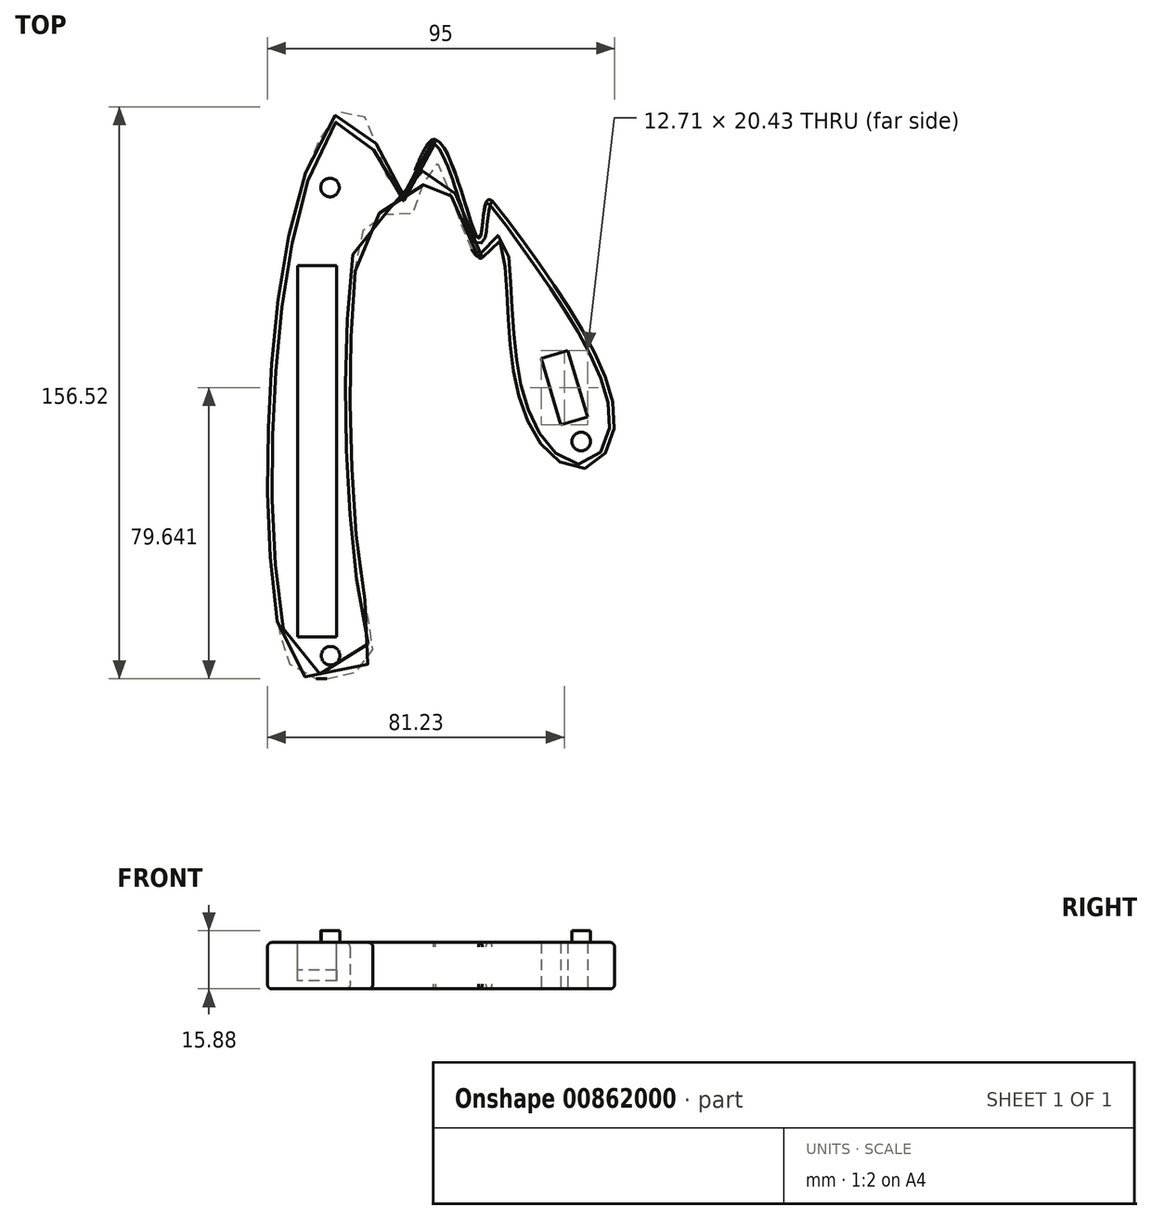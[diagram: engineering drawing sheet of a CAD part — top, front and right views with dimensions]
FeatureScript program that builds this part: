
annotation { "Feature Type Name" : "Feature", "Feature Type Description" : "" }
export const myFeature = defineFeature(function(context is Context, id is Id, definition is map)
    precondition{}
    {
        {
            var Q0;
            Q0=qCreatedBy(makeId("Top.planeOp"),FACE);
            var sketch = newSketch(context, id + "F0", { "sketchPlane" : qUnion([Q0])});
            skLineSegment(sketch, "E0", {"start": v(-51.7, -50.28) * mm, "end": v(-51.7, 51.32) * mm});
            skLineSegment(sketch, "E1", {"start": v(-51.7, 51.32) * mm, "end": v(-41.03, 51.32) * mm});
            skLineSegment(sketch, "E2", {"start": v(-41.03, 51.32) * mm, "end": v(-41.03, -50.28) * mm});
            skLineSegment(sketch, "E3", {"start": v(-41.03, -50.28) * mm, "end": v(-51.7, -50.28) * mm});
            skSolve(sketch);
        }
        {
            var Q0;
            Q0=qCreatedBy(makeId("Top.planeOp"),FACE);
            var sketch = newSketch(context, id + "F1", { "sketchPlane" : qUnion([Q0])});
            skFitSpline(sketch, "E4", {"points": [v(-54.86, -55.33) * mm, v(-52.7, 65.69) * mm, v(-34.43, 93.54) * mm, v(-23.53, 70.04) * mm, v(-14.05, 85.92) * mm, v(-2.09, 58.63) * mm, v(0, 68.77) * mm, v(6.48, 62.94) * mm, v(35.03, 10.86) * mm, v(26.31, -4.27) * mm, v(11.44, 8.55) * mm, v(5.44, 46.42) * mm, v(2.92, 58.25) * mm, v(-1.95, 53.46) * mm, v(-14.2, 80.06) * mm, v(-21.02, 64.6) * mm, v(-29.48, 65.69) * mm, v(-36.6, 40.93) * mm, v(-33.5, -38.92) * mm, v(-32.51, -57.76) * mm, v(-46.37, -61.66) * mm, v(-54.86, -55.33) * mm]});
            skLineSegment(sketch, "E5", {"start": v(20.37, 7.75) * mm, "end": v(27.68, 9.9) * mm});
            skLineSegment(sketch, "E6", {"start": v(27.68, 9.9) * mm, "end": v(22.28, 28.18) * mm});
            skLineSegment(sketch, "E7", {"start": v(22.28, 28.18) * mm, "end": v(14.98, 26.02) * mm});
            skLineSegment(sketch, "E8", {"start": v(14.98, 26.02) * mm, "end": v(20.37, 7.75) * mm});
            skCircle(sketch, "E9", {"center": v(-42.76, 72.74) * mm, "radius": 2.54 * mm});
            skCircle(sketch, "E10", {"center": v(25.96, 3.22) * mm, "radius": 2.54 * mm});
            skCircle(sketch, "E11", {"center": v(-42.62, -55.4) * mm, "radius": 2.54 * mm});
            skSolve(sketch);
        }
        {
            var Q0;
            Q0=makeQuery(id+"F1.imprint","IMPRINT",FACE,{"disambiguationData":[TD([[makeQuery(id+"F1.imprint","IMPRINT",EDGE,{"derivedFrom":sQuery(id+"F1.wireOp",EDGE,"E4")}),-1.0]])]});
            extrude(context, id + "F2", {"entities" : qUnion([Q0]), "endBound" : BoundingType.SYMMETRIC, "depth" : 12.7 * mm, "offsetDistance" : 25.4 * mm});
        }
        {
            var Q0;
            Q0 = qSketchRegion(id + "F0", true);
            extrude(context, id + "F3", {"entities" : qUnion([Q0]), "operationType" : NewBodyOperationType.REMOVE, "endBound" : BoundingType.SYMMETRIC, "oppositeDirection" : true, "depth" : 12.7 * mm, "offsetDistance" : 25.4 * mm});
        }
        {
            var Q0;
            Q0=makeQuery(id+"F2.opExtrude","CAP_EDGE",EDGE,{"disambiguationData":[OSD([sQuery(id+"F1.wireOp",EDGE,"E4")])],"isStart":false});
            fillet(context, id + "F4", {"entities" : qUnion([Q0]), "radius" : 1.27 * mm, "tangentPropagation" : true, "allowEdgeOverflow" : false});
        }
        {
            var Q0;
            Q0=makeQuery(id+"F2.opExtrude","CAP_EDGE",EDGE,{"disambiguationData":[OSD([sQuery(id+"F1.wireOp",EDGE,"E4")])],"isStart":true});
            fillet(context, id + "F5", {"entities" : qUnion([Q0]), "radius" : 1.27 * mm, "tangentPropagation" : true, "allowEdgeOverflow" : false});
        }
        {
            var Q0;
            Q0=makeQuery(id+"F1.imprint","IMPRINT",FACE,{"disambiguationData":[TD([[makeQuery(id+"F1.imprint","IMPRINT",EDGE,{"derivedFrom":sQuery(id+"F1.wireOp",EDGE,"E11")}),1.0]])]});
            var Q1;
            Q1=makeQuery(id+"F1.imprint","IMPRINT",FACE,{"disambiguationData":[TD([[makeQuery(id+"F1.imprint","IMPRINT",EDGE,{"derivedFrom":sQuery(id+"F1.wireOp",EDGE,"E9")}),1.0]])]});
            var Q2;
            Q2=makeQuery(id+"F1.imprint","IMPRINT",FACE,{"disambiguationData":[TD([[makeQuery(id+"F1.imprint","IMPRINT",EDGE,{"derivedFrom":sQuery(id+"F1.wireOp",EDGE,"E10")}),1.0]])]});
            var Q3;
            Q3=makeQuery(id+"F2.opExtrude","CAP_FACE",FACE,{"disambiguationData":[OSD([sQuery(id+"F1.wireOp",EDGE,"E4"),sQuery(id+"F1.wireOp",EDGE,"E5"),sQuery(id+"F1.wireOp",EDGE,"E6"),sQuery(id+"F1.wireOp",EDGE,"E7"),sQuery(id+"F1.wireOp",EDGE,"E8"),sQuery(id+"F1.wireOp",EDGE,"E9"),sQuery(id+"F1.wireOp",EDGE,"E10"),sQuery(id+"F1.wireOp",EDGE,"E11")])],"isStart":true});
            extrude(context, id + "F6", {"entities" : qUnion([Q0, Q1, Q2]), "operationType" : NewBodyOperationType.ADD, "endBound" : BoundingType.UP_TO_SURFACE, "oppositeDirection" : true, "depth" : 25.4 * mm, "endBoundEntityFace" : qUnion([Q3]), "offsetDistance" : 25.4 * mm, "hasSecondDirection" : true, "secondDirectionOppositeDirection" : false, "secondDirectionDepth" : 9.52 * mm});
        }
        {
            var Q0;
            Q0=makeQuery(id+"F3.boolean.opBoolean","COPY",FACE,{"derivedFrom":makeQuery(id+"F3.opExtrude","SWEPT_FACE",FACE,{"disambiguationData":[OSD([sQuery(id+"F0.wireOp",EDGE,"E0")])]})});
            var sketch = newSketch(context, id + "F7", { "sketchPlane" : qUnion([Q0])});
            skLineSegment(sketch, "E12", {"start": v(-50.28, -4.2) * mm, "end": v(51.32, -1.27) * mm});
            skLineSegment(sketch, "E13", {"start": v(51.32, -1.27) * mm, "end": v(51.32, -6.35) * mm});
            skLineSegment(sketch, "E14", {"start": v(51.32, -6.35) * mm, "end": v(-50.28, -6.35) * mm});
            skLineSegment(sketch, "E15", {"start": v(-50.28, -6.35) * mm, "end": v(-50.28, -4.2) * mm});
            skSolve(sketch);
        }
        {
            var Q0;
            Q0=makeQuery(id+"F7.imprint","IMPRINT",FACE,{"disambiguationData":[TD([[makeQuery(id+"F7.imprint","IMPRINT",EDGE,{"derivedFrom":sQuery(id+"F7.wireOp",EDGE,"E12")}),-1.0]])]});
            var Q1;
            Q1=makeQuery(id+"F3.boolean.opBoolean","COPY",FACE,{"derivedFrom":makeQuery(id+"F3.opExtrude","SWEPT_FACE",FACE,{"disambiguationData":[OSD([sQuery(id+"F0.wireOp",EDGE,"E2")])]})});
            extrude(context, id + "F8", {"entities" : qUnion([Q0]), "operationType" : NewBodyOperationType.ADD, "endBound" : BoundingType.UP_TO_SURFACE, "depth" : 25.4 * mm, "endBoundEntityFace" : qUnion([Q1]), "offsetDistance" : 25.4 * mm});
        }
    });
